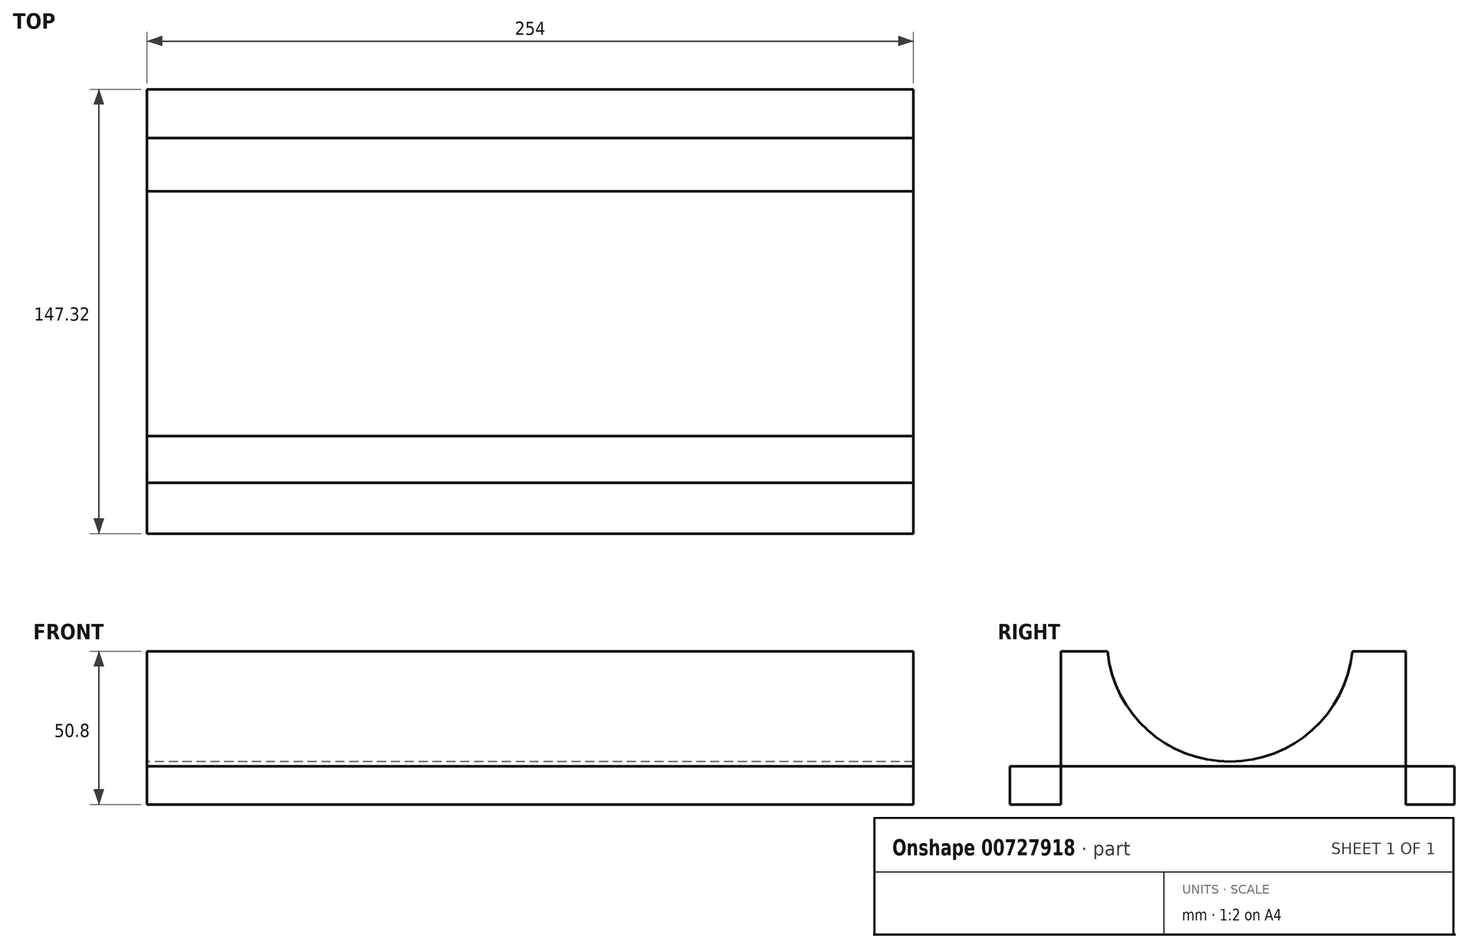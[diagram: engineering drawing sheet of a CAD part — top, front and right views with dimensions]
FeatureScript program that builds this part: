
annotation { "Feature Type Name" : "Feature", "Feature Type Description" : "" }
export const myFeature = defineFeature(function(context is Context, id is Id, definition is map)
    precondition{}
    {
        {
            var Q0;
            Q0=qCreatedBy(makeId("Right.planeOp"),FACE);
            var sketch = newSketch(context, id + "F0", { "sketchPlane" : qUnion([Q0])});
            skLineSegment(sketch, "E0.bottom", {"start": v(-73.66, 6.35) * mm, "end": v(73.66, 6.35) * mm});
            skLineSegment(sketch, "E0.top", {"start": v(-73.66, -6.35) * mm, "end": v(73.66, -6.35) * mm});
            skLineSegment(sketch, "E0.left", {"start": v(-73.66, 6.35) * mm, "end": v(-73.66, -6.35) * mm});
            skLineSegment(sketch, "E0.right", {"start": v(73.66, 6.35) * mm, "end": v(73.66, -6.35) * mm});
            skPoint(sketch, "E0.middle", {"position": v(0, 0) * mm});
            skLineSegment(sketch, "E1.bottom", {"start": v(-56.87, -6.35) * mm, "end": v(57.43, -6.35) * mm});
            skLineSegment(sketch, "E1.left", {"start": v(-56.87, -6.35) * mm, "end": v(-56.87, 44.45) * mm});
            skLineSegment(sketch, "E1.right", {"start": v(57.43, -6.35) * mm, "end": v(57.43, 44.45) * mm});
            skArc(sketch, "E2", {"start": v(-41.4, 44.45) * mm, "mid": v(-0.8, 7.84) * mm, "end": v(39.78, 44.45) * mm});
            skLineSegment(sketch, "E3", {"start": v(-56.87, 44.45) * mm, "end": v(-41.4, 44.45) * mm});
            skLineSegment(sketch, "E4", {"start": v(39.78, 44.45) * mm, "end": v(57.43, 44.45) * mm});
            skSolve(sketch);
        }
        {
            var Q0;
            {var subQ8=sQuery(id+"F0.wireOp",EDGE,"E2");Q0=makeQuery(id+"F0.imprint","IMPRINT",FACE,{"disambiguationData":[TD([[makeQuery(id+"F0.imprint","IMPRINT",EDGE,{"derivedFrom":subQ8}),-1.0]])]});}
            var Q1;
            {var subQ0=sQuery(id+"F0.wireOp",EDGE,"E2");Q1=makeQuery(id+"F0.imprint","IMPRINT",FACE,{"disambiguationData":[TD([[makeQuery(id+"F0.imprint","IMPRINT",EDGE,{"derivedFrom":subQ0}),1.0]])]});}
            var Q2;
            {var subQ5=sQuery(id+"F0.wireOp",EDGE,"E1.bottom");Q2=makeQuery(id+"F0.imprint","IMPRINT",FACE,{"disambiguationData":[TD([[makeQuery(id+"F0.imprint","IMPRINT",EDGE,{"derivedFrom":subQ5}),1.0]])]});}
            var Q3;
            {var subQ0=sQuery(id+"F0.wireOp",EDGE,"E0.right");Q3=makeQuery(id+"F0.imprint","IMPRINT",FACE,{"disambiguationData":[TD([[makeQuery(id+"F0.imprint","IMPRINT",EDGE,{"derivedFrom":subQ0}),-1.0]])]});}
            var Q4;
            {var subQ0=sQuery(id+"F0.wireOp",EDGE,"E0.left");Q4=makeQuery(id+"F0.imprint","IMPRINT",FACE,{"disambiguationData":[TD([[makeQuery(id+"F0.imprint","IMPRINT",EDGE,{"derivedFrom":subQ0}),1.0]])]});}
            extrude(context, id + "F1", {"entities" : qUnion([Q0, Q1, Q2, Q3, Q4]), "depth" : 254 * mm, "offsetDistance" : 25.4 * mm});
        }
    });
